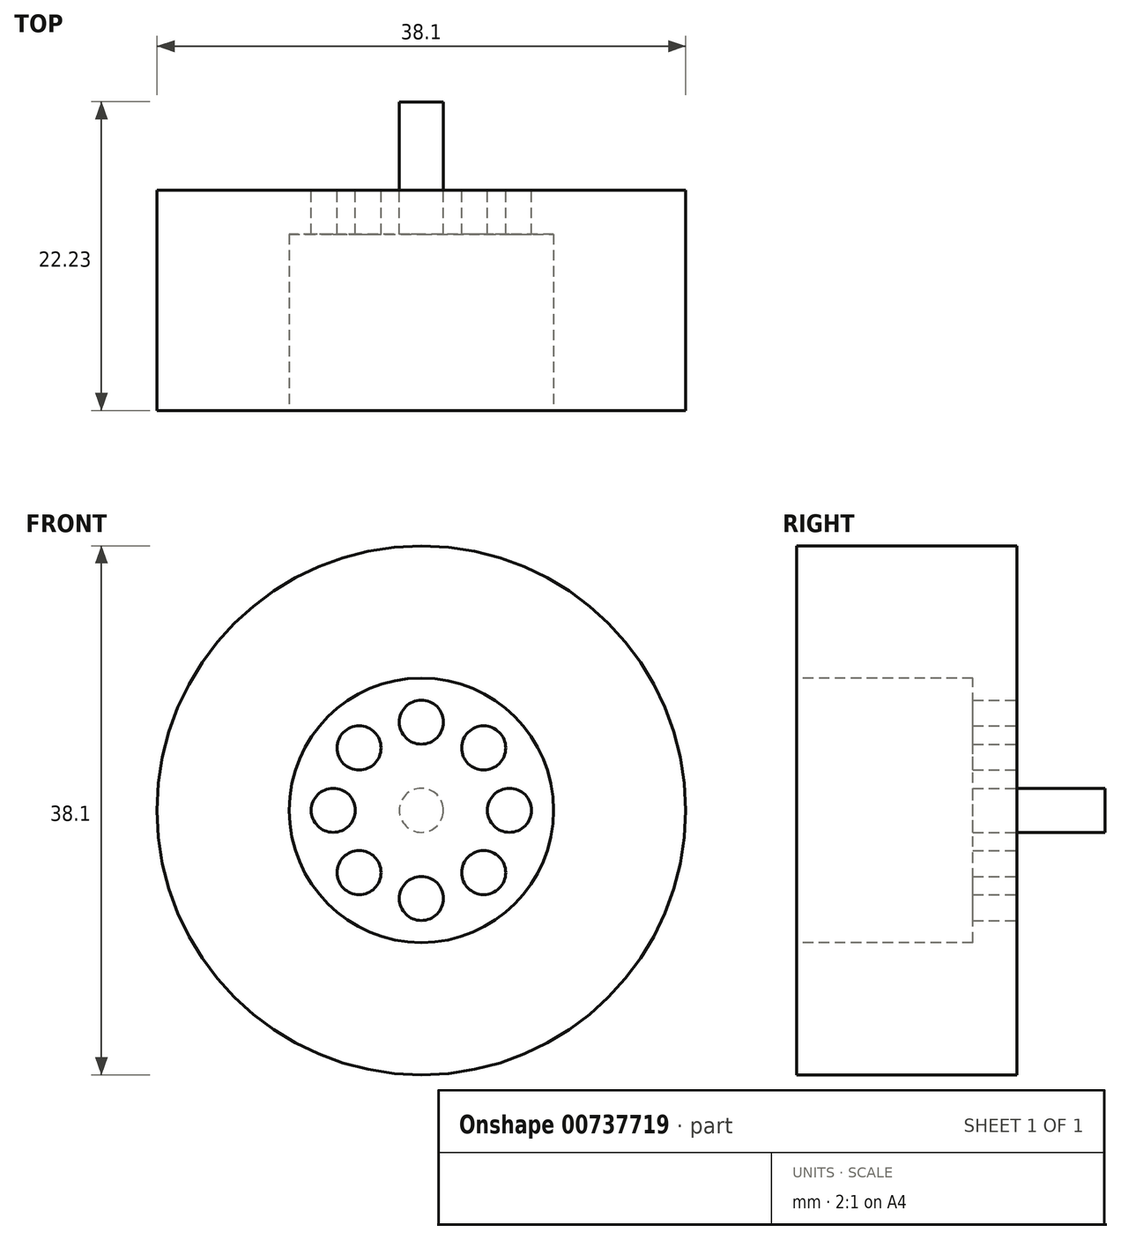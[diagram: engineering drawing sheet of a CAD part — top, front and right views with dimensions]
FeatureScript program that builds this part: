
annotation { "Feature Type Name" : "Feature", "Feature Type Description" : "" }
export const myFeature = defineFeature(function(context is Context, id is Id, definition is map)
    precondition{}
    {
        {
            var Q0;
            Q0=qCreatedBy(makeId("Front.planeOp"),FACE);
            var sketch = newSketch(context, id + "F0", { "sketchPlane" : qUnion([Q0])});
            skCircle(sketch, "E0", {"center": v(0, 0) * mm, "radius": 19.05 * mm});
            skSolve(sketch);
        }
        {
            var Q0;
            Q0=makeQuery(id+"F0.imprint","IMPRINT",FACE,{"disambiguationData":[TD([[makeQuery(id+"F0.imprint","IMPRINT",EDGE,{"derivedFrom":sQuery(id+"F0.wireOp",EDGE,"E0")}),1.0]])]});
            extrude(context, id + "F1", {"entities" : qUnion([Q0]), "oppositeDirection" : true, "depth" : 15.88 * mm, "offsetDistance" : 25.4 * mm});
        }
        {
            var Q0;
            Q0=makeQuery(id+"F1.opExtrude","CAP_FACE",FACE,{"disambiguationData":[OSD([sQuery(id+"F0.wireOp",EDGE,"E0")])],"isStart":true});
            var sketch = newSketch(context, id + "F2", { "sketchPlane" : qUnion([Q0])});
            skCircle(sketch, "E1", {"center": v(0, 0) * mm, "radius": 9.53 * mm});
            skSolve(sketch);
        }
        {
            var Q0;
            Q0=makeQuery(id+"F2.imprint","IMPRINT",FACE,{"disambiguationData":[TD([[makeQuery(id+"F2.imprint","IMPRINT",EDGE,{"derivedFrom":sQuery(id+"F2.wireOp",EDGE,"E1")}),1.0]])]});
            extrude(context, id + "F3", {"entities" : qUnion([Q0]), "operationType" : NewBodyOperationType.REMOVE, "oppositeDirection" : true, "depth" : 12.7 * mm, "offsetDistance" : 25.4 * mm});
        }
        {
            var Q0;
            Q0=makeQuery(id+"F1.opExtrude","CAP_FACE",FACE,{"disambiguationData":[OSD([sQuery(id+"F0.wireOp",EDGE,"E0")])],"isStart":false});
            var sketch = newSketch(context, id + "F4", { "sketchPlane" : qUnion([Q0])});
            skCircle(sketch, "E2", {"center": v(0, 0) * mm, "radius": 9.53 * mm});
            skSolve(sketch);
        }
        {
            var Q0;
            Q0=makeQuery(id+"F3.boolean.opBoolean","COPY",FACE,{"derivedFrom":makeQuery(id+"F3.opExtrude","CAP_FACE",FACE,{"disambiguationData":[OSD([sQuery(id+"F2.wireOp",EDGE,"E1")])],"isStart":false})});
            var sketch = newSketch(context, id + "F5", { "sketchPlane" : qUnion([Q0])});
            skCircle(sketch, "E3", {"center": v(0, 0) * mm, "radius": 1.59 * mm});
            skSolve(sketch);
        }
        {
            var Q0;
            Q0=makeQuery(id+"F5.imprint","IMPRINT",FACE,{"disambiguationData":[TD([[makeQuery(id+"F5.imprint","IMPRINT",EDGE,{"derivedFrom":sQuery(id+"F5.wireOp",EDGE,"E3")}),1.0]])]});
            extrude(context, id + "F6", {"entities" : qUnion([Q0]), "operationType" : NewBodyOperationType.ADD, "oppositeDirection" : true, "depth" : 9.52 * mm, "offsetDistance" : 25.4 * mm});
        }
        {
            var Q0;
            Q0=makeQuery(id+"F4.imprint","IMPRINT",FACE,{"disambiguationData":[TD([[makeQuery(id+"F4.imprint","IMPRINT",EDGE,{"derivedFrom":sQuery(id+"F4.wireOp",EDGE,"E2")}),1.0]])]});
            var sketch = newSketch(context, id + "F7", { "sketchPlane" : qUnion([Q0])});
            skCircle(sketch, "E4", {"center": v(0, 6.35) * mm, "radius": 1.59 * mm});
            skCircle(sketch, "E5.1.0", {"center": v(-4.5, 4.5) * mm, "radius": 1.59 * mm});
            skCircle(sketch, "E5.2.0", {"center": v(-6.35, 0) * mm, "radius": 1.59 * mm});
            skCircle(sketch, "E5.3.0", {"center": v(-4.5, -4.5) * mm, "radius": 1.59 * mm});
            skCircle(sketch, "E5.4.0", {"center": v(0, -6.35) * mm, "radius": 1.59 * mm});
            skCircle(sketch, "E5.5.0", {"center": v(4.5, -4.5) * mm, "radius": 1.59 * mm});
            skCircle(sketch, "E5.6.0", {"center": v(6.35, 0) * mm, "radius": 1.59 * mm});
            skCircle(sketch, "E5.7.0", {"center": v(4.5, 4.5) * mm, "radius": 1.59 * mm});
            skPoint(sketch, "E5.center", {"position": v(0, 0) * mm});
            skSolve(sketch);
        }
        {
            var Q0;
            Q0 = qSketchRegion(id + "F7", true);
            extrude(context, id + "F8", {"entities" : qUnion([Q0]), "operationType" : NewBodyOperationType.REMOVE, "oppositeDirection" : true, "depth" : 25.4 * mm, "offsetDistance" : 25.4 * mm});
        }
    });
